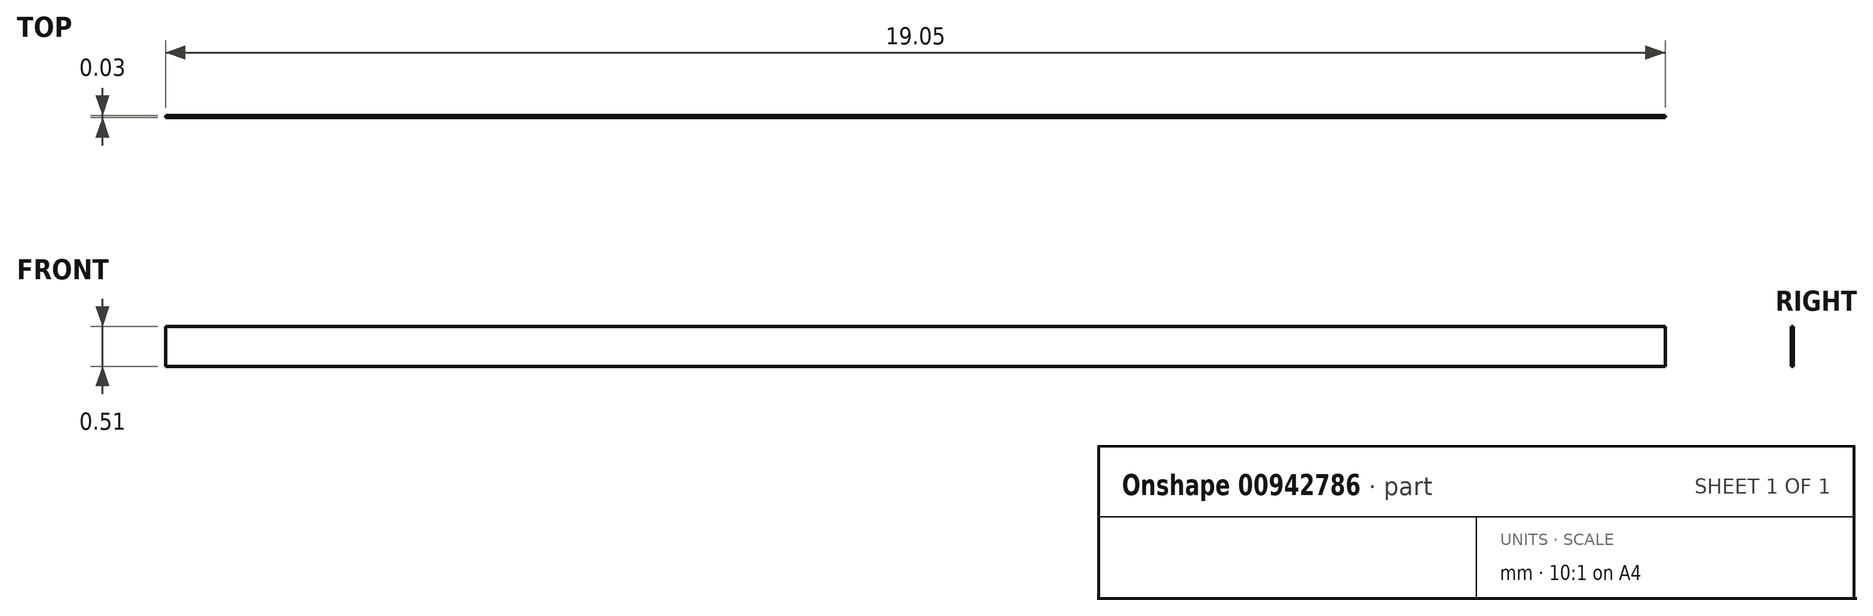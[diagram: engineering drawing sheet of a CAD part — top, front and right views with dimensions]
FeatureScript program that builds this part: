
annotation { "Feature Type Name" : "Feature", "Feature Type Description" : "" }
export const myFeature = defineFeature(function(context is Context, id is Id, definition is map)
    precondition{}
    {
        {
            var Q0;
            Q0=qCreatedBy(makeId("Front.planeOp"),FACE);
            var sketch = newSketch(context, id + "F0", { "sketchPlane" : qUnion([Q0])});
            skLineSegment(sketch, "E0.bottom", {"start": v(0, 0) * mm, "end": v(19.05, 0) * mm});
            skLineSegment(sketch, "E0.top", {"start": v(0, 0.5) * mm, "end": v(19.05, 0.5) * mm});
            skLineSegment(sketch, "E0.left", {"start": v(0, 0) * mm, "end": v(0, 0.5) * mm});
            skLineSegment(sketch, "E0.right", {"start": v(19.05, 0) * mm, "end": v(19.05, 0.5) * mm});
            skSolve(sketch);
        }
        {
            var Q0;
            Q0=makeQuery(id+"F0.imprint","IMPRINT",FACE,{"disambiguationData":[TD([[makeQuery(id+"F0.imprint","IMPRINT",EDGE,{"derivedFrom":sQuery(id+"F0.wireOp",EDGE,"E0.bottom")}),1.0]])]});
            extrude(context, id + "F1", {"entities" : qUnion([Q0]), "depth" : 0.03 * mm, "offsetDistance" : 25.4 * mm});
        }
    });
